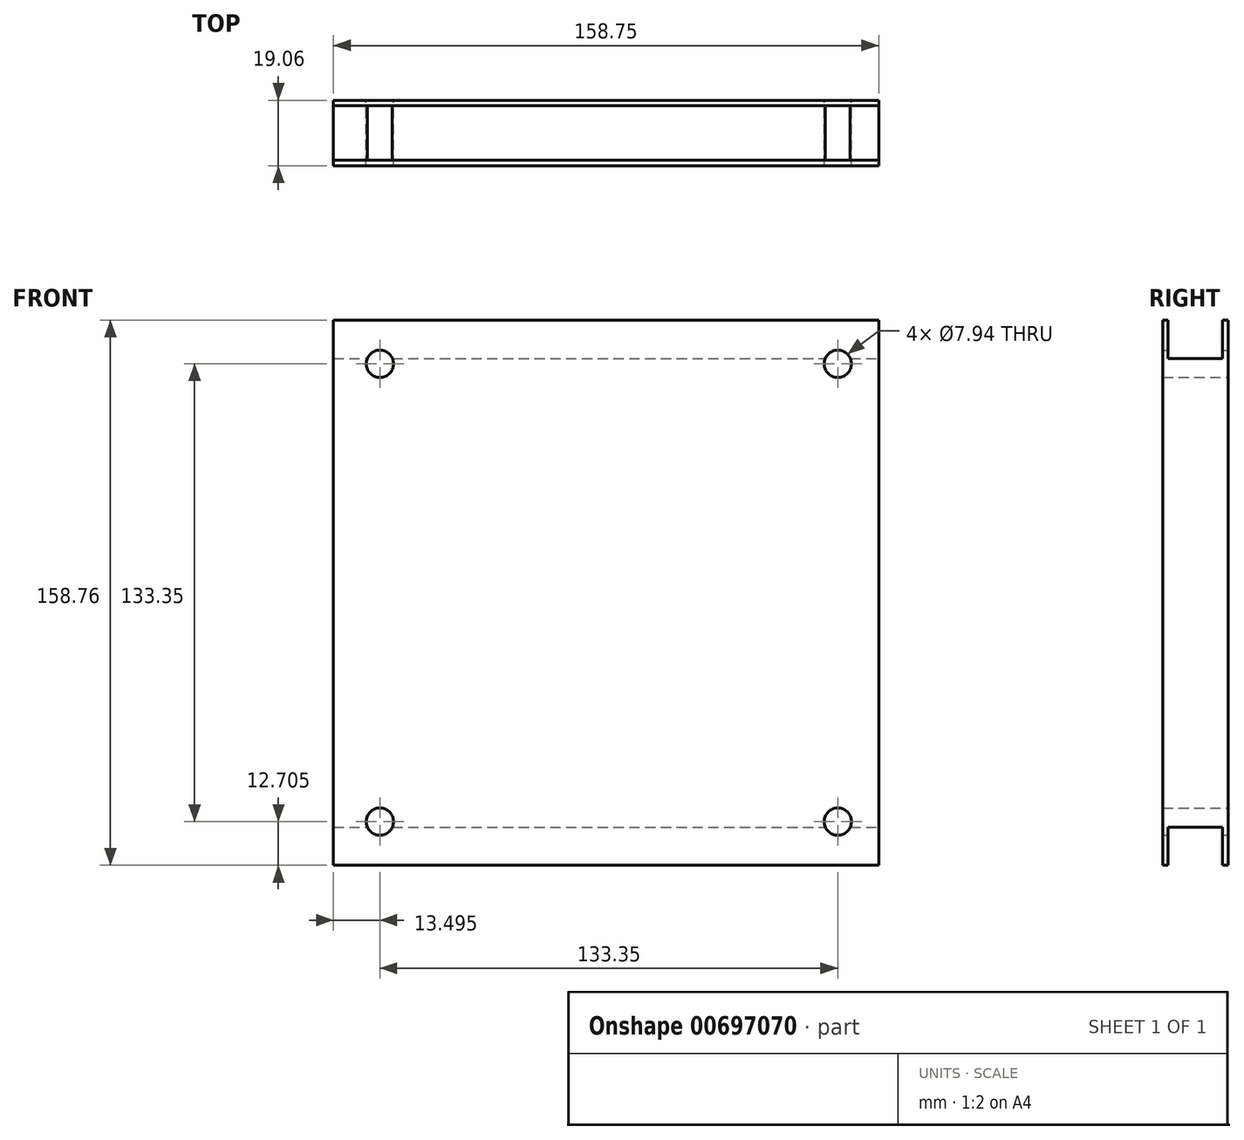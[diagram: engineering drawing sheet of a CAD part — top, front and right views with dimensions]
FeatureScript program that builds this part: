
annotation { "Feature Type Name" : "Feature", "Feature Type Description" : "" }
export const myFeature = defineFeature(function(context is Context, id is Id, definition is map)
    precondition{}
    {
        {
            var Q0;
            Q0=qCreatedBy(makeId("Right.planeOp"),FACE);
            cPlane(context, id + "F0", {"entities" : qUnion([Q0]), "cplaneType" : CPlaneType.OFFSET, "offset" : 78.58 * mm, "width" : 152.4 * mm, "height" : 152.4 * mm});
        }
        {
            var Q0;
            Q0=qCreatedBy(id+"F0.planeOp",FACE);
            var sketch = newSketch(context, id + "F1", { "sketchPlane" : qUnion([Q0])});
            skLineSegment(sketch, "E0", {"start": v(-9.52, 79.38) * mm, "end": v(-7.94, 79.38) * mm});
            skLineSegment(sketch, "E1", {"start": v(7.94, 79.38) * mm, "end": v(9.52, 79.38) * mm});
            skLineSegment(sketch, "E2", {"start": v(9.52, 79.37) * mm, "end": v(9.52, -79.37) * mm});
            skLineSegment(sketch, "E3", {"start": v(9.52, -79.38) * mm, "end": v(7.94, -79.38) * mm});
            skLineSegment(sketch, "E4", {"start": v(7.94, -79.38) * mm, "end": v(7.94, -68.26) * mm});
            skLineSegment(sketch, "E5", {"start": v(7.94, -68.26) * mm, "end": v(-7.94, -68.26) * mm});
            skLineSegment(sketch, "E6", {"start": v(-7.94, -68.26) * mm, "end": v(-7.94, -79.38) * mm});
            skLineSegment(sketch, "E7", {"start": v(-7.94, -79.38) * mm, "end": v(-9.53, -79.38) * mm});
            skLineSegment(sketch, "E8", {"start": v(-9.53, -79.38) * mm, "end": v(-9.53, 79.38) * mm});
            skLineSegment(sketch, "E9", {"start": v(0, -68.26) * mm, "end": v(0, 68.26) * mm, "construction": true});
            skLineSegment(sketch, "E10", {"start": v(-7.94, 79.38) * mm, "end": v(-7.94, 68.26) * mm});
            skLineSegment(sketch, "E11", {"start": v(-7.94, 68.26) * mm, "end": v(7.94, 68.26) * mm});
            skLineSegment(sketch, "E12", {"start": v(7.94, 68.26) * mm, "end": v(7.94, 79.38) * mm});
            skLineSegment(sketch, "E13", {"start": v(0, 0) * mm, "end": v(9.53, 0) * mm, "construction": true});
            skLineSegment(sketch, "E14", {"start": v(0, 0) * mm, "end": v(-9.53, 0) * mm, "construction": true});
            skSolve(sketch);
        }
        {
            var Q0;
            Q0 = qSketchRegion(id + "F1", true);
            extrude(context, id + "F2", {"entities" : qUnion([Q0]), "oppositeDirection" : true, "depth" : 158.75 * mm, "offsetDistance" : 25.4 * mm});
        }
        {
            var Q0;
            Q0=makeQuery(id+"F2.opExtrude","SWEPT_FACE",FACE,{"disambiguationData":[OSD([sQuery(id+"F1.wireOp",EDGE,"E2")])]});
            var sketch = newSketch(context, id + "F3", { "sketchPlane" : qUnion([Q0])});
            skLineSegment(sketch, "E15.bottom", {"start": v(66.68, 66.68) * mm, "end": v(-66.68, 66.68) * mm, "construction": true});
            skLineSegment(sketch, "E15.top", {"start": v(66.68, -66.68) * mm, "end": v(-66.68, -66.68) * mm, "construction": true});
            skLineSegment(sketch, "E15.left", {"start": v(66.68, 66.68) * mm, "end": v(66.68, -66.68) * mm, "construction": true});
            skLineSegment(sketch, "E15.right", {"start": v(-66.68, 66.68) * mm, "end": v(-66.68, -66.68) * mm, "construction": true});
            skPoint(sketch, "E15.middle", {"position": v(0, 0) * mm});
            skCircle(sketch, "E16", {"center": v(66.68, 66.68) * mm, "radius": 3.97 * mm});
            skCircle(sketch, "E17", {"center": v(-66.68, 66.68) * mm, "radius": 3.97 * mm});
            skCircle(sketch, "E18", {"center": v(-66.68, -66.68) * mm, "radius": 3.97 * mm});
            skCircle(sketch, "E19", {"center": v(66.68, -66.68) * mm, "radius": 3.97 * mm});
            skSolve(sketch);
        }
        {
            var Q0;
            Q0 = qSketchRegion(id + "F3", true);
            extrude(context, id + "F4", {"entities" : qUnion([Q0]), "operationType" : NewBodyOperationType.REMOVE, "endBound" : BoundingType.THROUGH_ALL, "oppositeDirection" : true, "depth" : 25.4 * mm, "offsetDistance" : 25.4 * mm});
        }
    });
